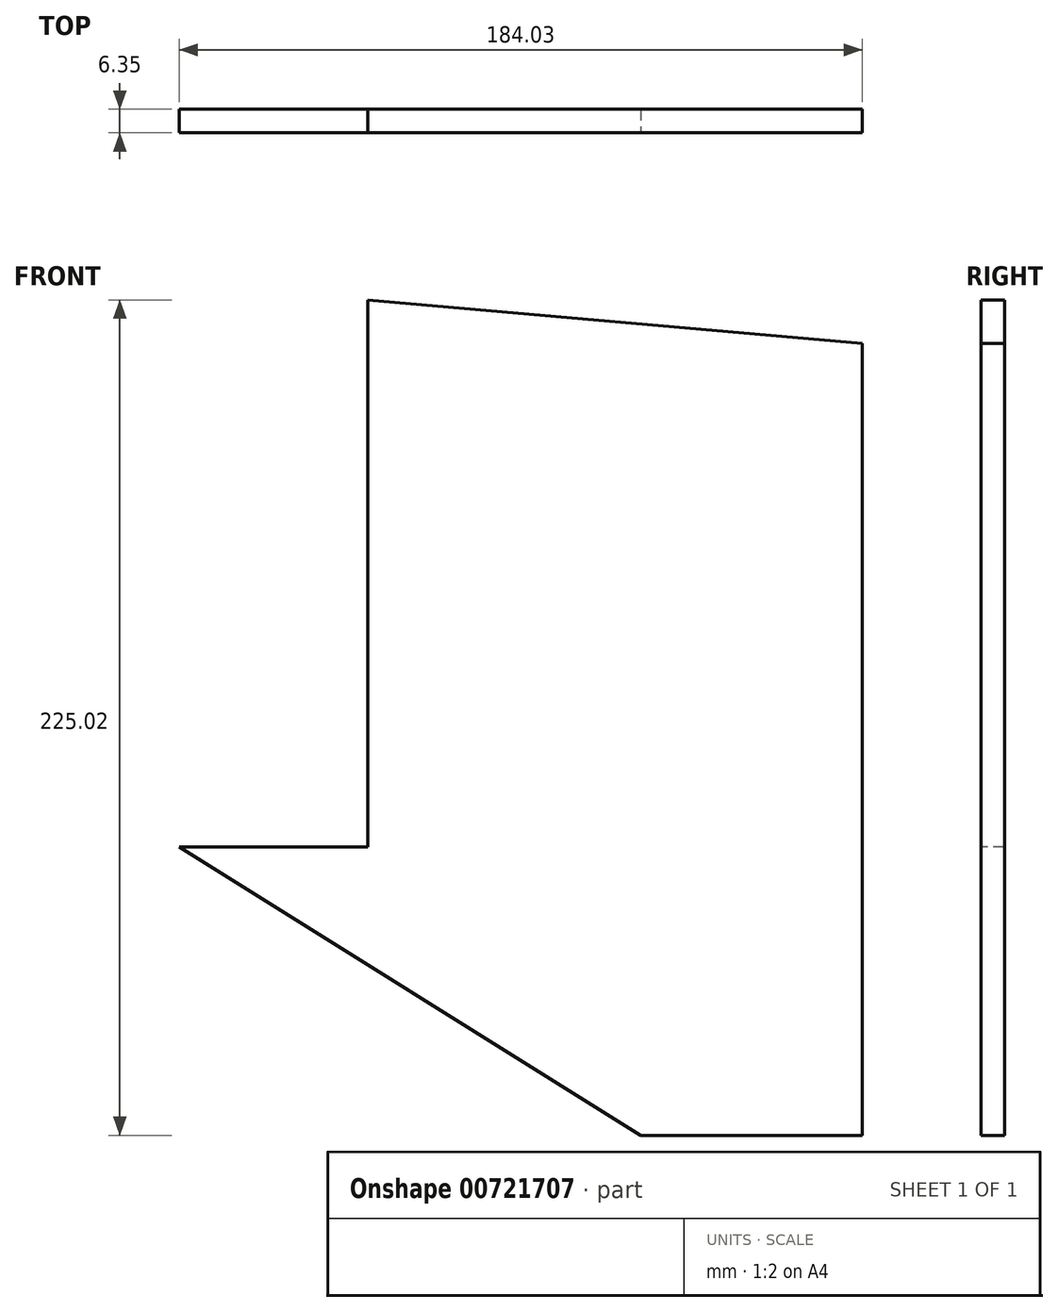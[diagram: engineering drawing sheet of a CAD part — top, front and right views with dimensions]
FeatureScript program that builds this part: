
annotation { "Feature Type Name" : "Feature", "Feature Type Description" : "" }
export const myFeature = defineFeature(function(context is Context, id is Id, definition is map)
    precondition{}
    {
        {
            var Q0;
            Q0=qCreatedBy(makeId("Front.planeOp"),FACE);
            var sketch = newSketch(context, id + "F0", { "sketchPlane" : qUnion([Q0])});
            skLineSegment(sketch, "E0", {"start": v(184.03, 135.66) * mm, "end": v(50.8, 147.32) * mm});
            skLineSegment(sketch, "E1", {"start": v(184.03, -77.7) * mm, "end": v(124.34, -77.7) * mm});
            skLineSegment(sketch, "E2", {"start": v(124.34, -77.7) * mm, "end": v(0, 0) * mm});
            skLineSegment(sketch, "E3", {"start": v(0, 0) * mm, "end": v(50.8, 0) * mm});
            skLineSegment(sketch, "E4", {"start": v(184.03, 135.66) * mm, "end": v(184.03, -77.7) * mm});
            skLineSegment(sketch, "E5", {"start": v(50.8, 0) * mm, "end": v(50.8, 147.32) * mm});
            skSolve(sketch);
        }
        {
            var Q0;
            Q0=qSketchRegion(id+"F0",true);
            extrude(context, id + "F1", {"entities" : qUnion([Q0]), "oppositeDirection" : true, "depth" : 6.35 * mm, "offsetDistance" : 25.4 * mm});
        }
    });
